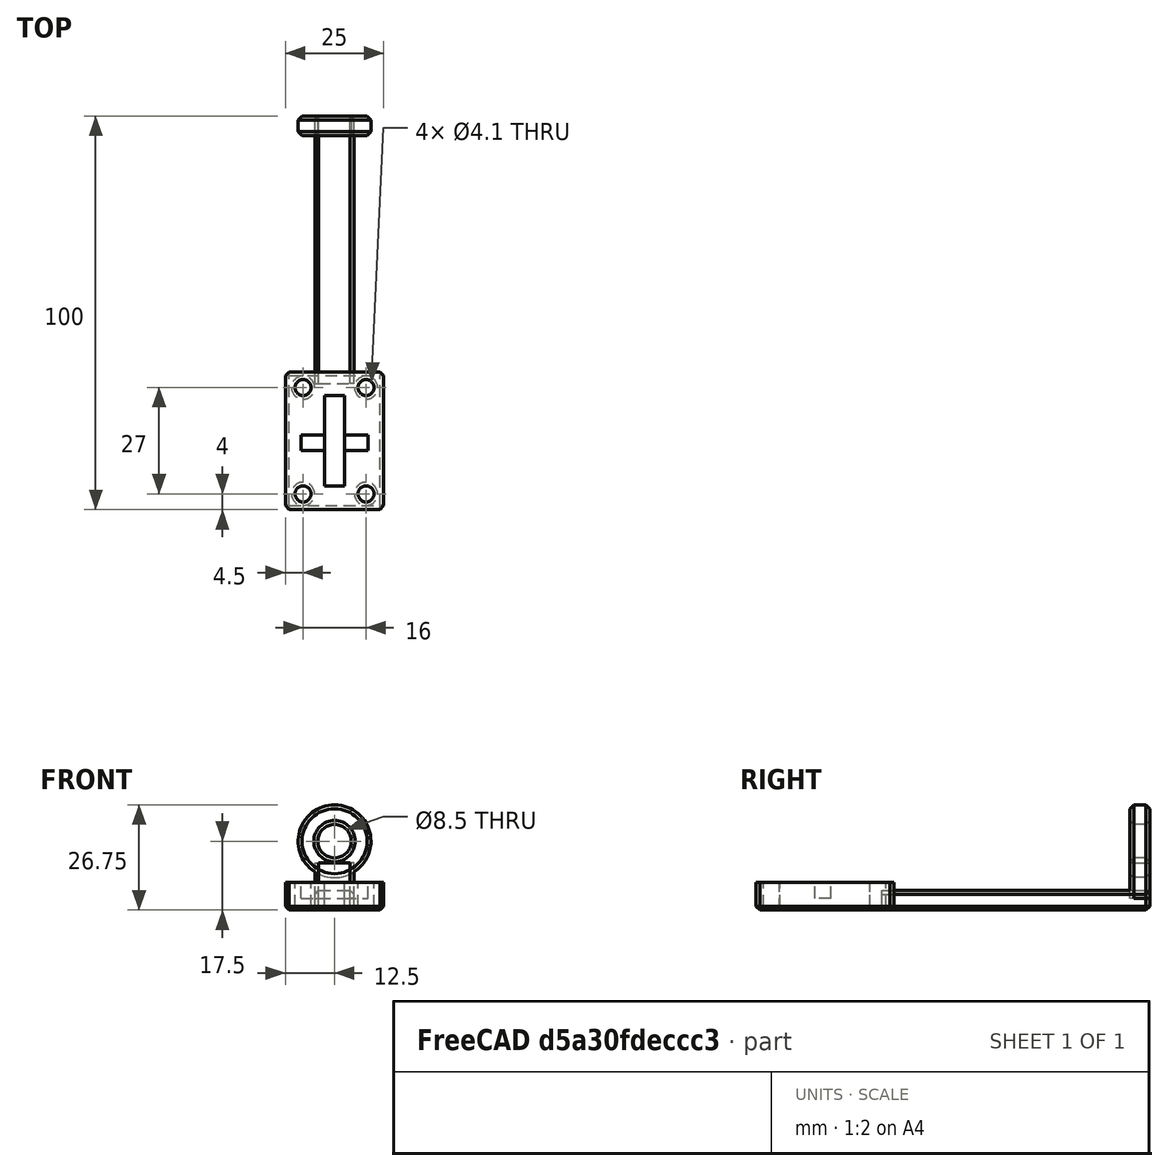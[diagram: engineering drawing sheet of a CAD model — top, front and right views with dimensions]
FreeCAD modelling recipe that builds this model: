
FCSTD DOCUMENT  (FreeCAD 0.16R)
Label: filament-führung_version_1.2
License: All rights reserved
LicenseURL: http://en.wikipedia.org/wiki/All_rights_reserved
objects: Part::Cut×7, Part::Cylinder×6, Part::Chamfer×6, Part::Box×5
note: 24 computed .brp shape members not serialized (recipe doc carries the construction recipe); baked Part::Feature solids carry a one-line shape summary decoded from their .brp

FEATURE [Part::Box] Box  label="Cube"
  Height = 7
  Length = 25
  Width = 35
FEATURE [Part::Box] Box001  label="Cube001"
  Height = 5
  Length = 10
  Placement = pos=(7.5,32,0) rot=(0,0,1;0rad)
  Width = 68
FEATURE [Part::Box] Box002  label="Cube002"
  Height = 7
  Length = 5
  Placement = pos=(10,6,0) rot=(0,0,1;0rad)
  Width = 23
FEATURE [Part::Cut] Cut
  Base = -> Box
  Tool = -> Box002
FEATURE [Part::Cylinder] Cylinder  label="Cylinder000"
  Angle = 360
  Height = 7
  Placement = pos=(4.5,4,0) rot=(0,0,1;0rad)
  Radius = 2.05
FEATURE [Part::Cylinder] Cylinder001
  Angle = 360
  Height = 7
  Placement = pos=(4.5,31,0) rot=(0,0,1;0rad)
  Radius = 2.05
FEATURE [Part::Cylinder] Cylinder002
  Angle = 360
  Height = 7
  Placement = pos=(20.5,31,0) rot=(0,0,1;0rad)
  Radius = 2.05
FEATURE [Part::Cylinder] Cylinder003
  Angle = 360
  Height = 7
  Placement = pos=(20.5,4,0) rot=(0,0,1;0rad)
  Radius = 2.05
FEATURE [Part::Cut] Cut001
  Base = -> Cut
  Tool = -> Cylinder
FEATURE [Part::Cut] Cut002
  Base = -> Cut001
  Tool = -> Cylinder001
FEATURE [Part::Cut] Cut003
  Base = -> Cut002
  Tool = -> Cylinder002
FEATURE [Part::Cut] Cut004
  Base = -> Cut003
  Tool = -> Cylinder003
FEATURE [Part::Box] Box003  label="Cube003"
  Height = 9
  Length = 10
  Placement = pos=(7.5,95,3) rot=(0,0,1;0rad)
  Width = 5
FEATURE [Part::Cylinder] Cylinder004  label="Cylinder"
  Angle = 360
  Height = 5
  Placement = pos=(12.5,100,17.5) rot=(1,0,0;1.5708rad)
  Radius = 4.25
FEATURE [Part::Cylinder] Cylinder005  label="Cylinder004"
  Angle = 360
  Height = 5
  Placement = pos=(12.5,100,17.5) rot=(1,0,0;1.5708rad)
  Radius = 9.25
FEATURE [Part::Cut] Cut005
  Base = -> Cylinder005
  Tool = -> Cylinder004
FEATURE [Part::Chamfer] Chamfer
  Base = -> Cut005
  Edges = 4 edges r=1: [Edge1,Edge3,Edge4,Edge5]
FEATURE [Part::Chamfer] Chamfer001
  Base = -> Box003
  Edges = 4 edges r=1: [Edge1,Edge3,Edge5,Edge7]
FEATURE [Part::Chamfer] Chamfer002
  Base = -> Box001
  Edges = 7 edges r=1: [Edge2,Edge3,Edge4,Edge6,Edge7,Edge8,Edge11]
FEATURE [Part::Chamfer] Chamfer003
  Base = -> Cut004
  Edges = 8 edges r=1: [Edge1,Edge3,Edge4,Edge5,Edge6,Edge18,Edge19,Edge20]
FEATURE [Part::Box] Box004  label="Cube004"
  Height = 4
  Length = 17
  Placement = pos=(4,15,3) rot=(0,0,1;0rad)
  Width = 4
FEATURE [Part::Cut] Cut006
  Base = -> Chamfer003
  Tool = -> Box004
FEATURE [Part::Chamfer] Chamfer004
  Base = -> Cut006
  Edges = 1 edges r=0.9: [Edge47]
FEATURE [Part::Chamfer] Chamfer005
  Base = -> Chamfer004
  Edges = 3 edges r=0.9: [Edge33,Edge34,Edge39]
